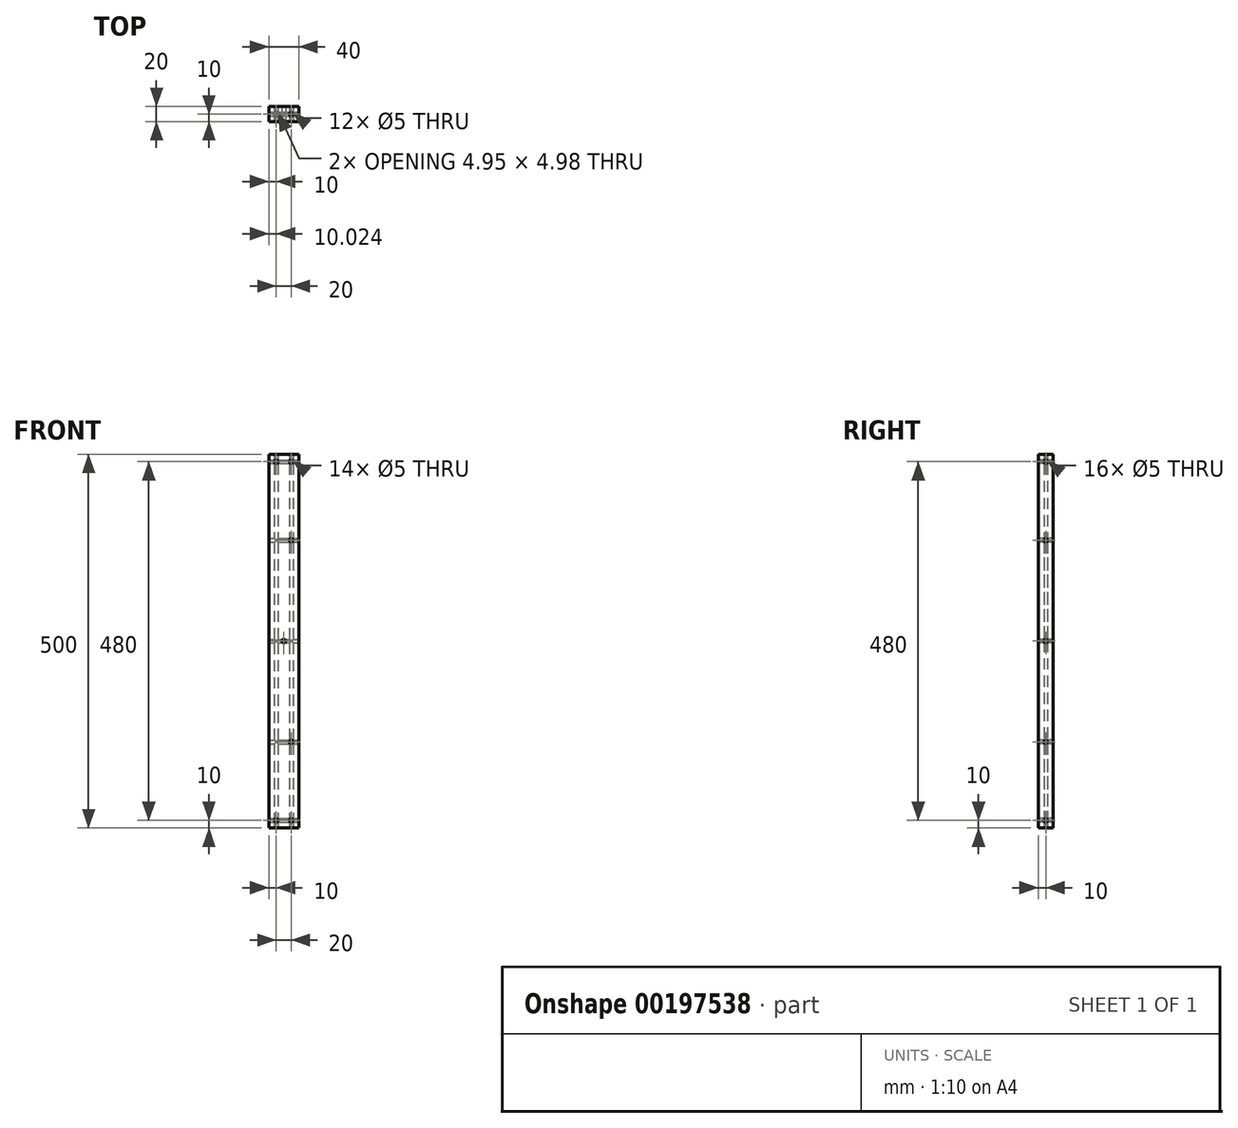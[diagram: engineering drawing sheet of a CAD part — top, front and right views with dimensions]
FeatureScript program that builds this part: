
annotation { "Feature Type Name" : "Feature", "Feature Type Description" : "" }
export const myFeature = defineFeature(function(context is Context, id is Id, definition is map)
    precondition{}
    {
        {
            var Q0;
            Q0=qCreatedBy(makeId("Top.planeOp"),FACE);
            var sketch = newSketch(context, id + "F0", { "sketchPlane" : qUnion([Q0])});
            skLineSegment(sketch, "E0.bottom", {"start": v(-20, 10) * mm, "end": v(20, 10) * mm});
            skLineSegment(sketch, "E0.top", {"start": v(-20, -10) * mm, "end": v(20, -10) * mm});
            skLineSegment(sketch, "E0.left", {"start": v(-20, 10) * mm, "end": v(-20, -10) * mm});
            skLineSegment(sketch, "E0.right", {"start": v(20, 10) * mm, "end": v(20, -10) * mm});
            skCircle(sketch, "E1", {"center": v(-10, 0) * mm, "radius": 2.5 * mm});
            skCircle(sketch, "E2", {"center": v(10, 0) * mm, "radius": 2.5 * mm});
            skSolve(sketch);
        }
        {
            var Q0;
            Q0=qSketchRegion(id+"F0",true);
            extrude(context, id + "F1", {"entities" : qUnion([Q0]), "depth" : 500 * mm});
        }
        {
            var Q0;
            Q0=makeQuery(id+"F1.opExtrude","SWEPT_FACE",FACE,{"disambiguationData":[OSD([sQuery(id+"F0.wireOp",EDGE,"E0.right")])]});
            var sketch = newSketch(context, id + "F2", { "sketchPlane" : qUnion([Q0])});
            skCircle(sketch, "E3", {"center": v(0, 10) * mm, "radius": 2.5 * mm});
            skCircle(sketch, "E4", {"center": v(0, 490) * mm, "radius": 2.5 * mm});
            skCircle(sketch, "E5", {"center": v(0, 250) * mm, "radius": 2.5 * mm});
            skPoint(sketch, "E5.centerSnap0", {"position": v(-10, 250) * mm});
            skCircle(sketch, "E6", {"center": v(0, 115.13) * mm, "radius": 2.5 * mm});
            skCircle(sketch, "E7", {"center": v(0, 384.87) * mm, "radius": 2.5 * mm});
            skSolve(sketch);
        }
        {
            var Q0;
            Q0=qSketchRegion(id+"F2",true);
            extrude(context, id + "F3", {"entities" : qUnion([Q0]), "operationType" : NewBodyOperationType.REMOVE, "endBound" : BoundingType.THROUGH_ALL, "oppositeDirection" : true, "depth" : 25 * mm});
        }
        {
            var Q0;
            Q0=makeQuery(id+"F1.opExtrude","SWEPT_FACE",FACE,{"disambiguationData":[OSD([sQuery(id+"F0.wireOp",EDGE,"E0.top")])]});
            var sketch = newSketch(context, id + "F4", { "sketchPlane" : qUnion([Q0])});
            skCircle(sketch, "E8", {"center": v(0, 250) * mm, "radius": 2.5 * mm});
            skPoint(sketch, "E8.centerSnap0", {"position": v(-20, 250) * mm});
            skCircle(sketch, "E9", {"center": v(-10, 490) * mm, "radius": 2.5 * mm});
            skCircle(sketch, "E10", {"center": v(10, 490) * mm, "radius": 2.5 * mm});
            skCircle(sketch, "E11", {"center": v(-10, 10) * mm, "radius": 2.5 * mm});
            skCircle(sketch, "E12", {"center": v(10, 10) * mm, "radius": 2.5 * mm});
            skCircle(sketch, "E13", {"center": v(10, 115.13) * mm, "radius": 2.5 * mm});
            skCircle(sketch, "E14", {"center": v(10, 384.87) * mm, "radius": 2.5 * mm});
            skSolve(sketch);
        }
        {
            var Q0;
            Q0=qSketchRegion(id+"F4",true);
            extrude(context, id + "F5", {"entities" : qUnion([Q0]), "operationType" : NewBodyOperationType.REMOVE, "endBound" : BoundingType.THROUGH_ALL, "oppositeDirection" : true, "depth" : 25 * mm});
        }
    });
